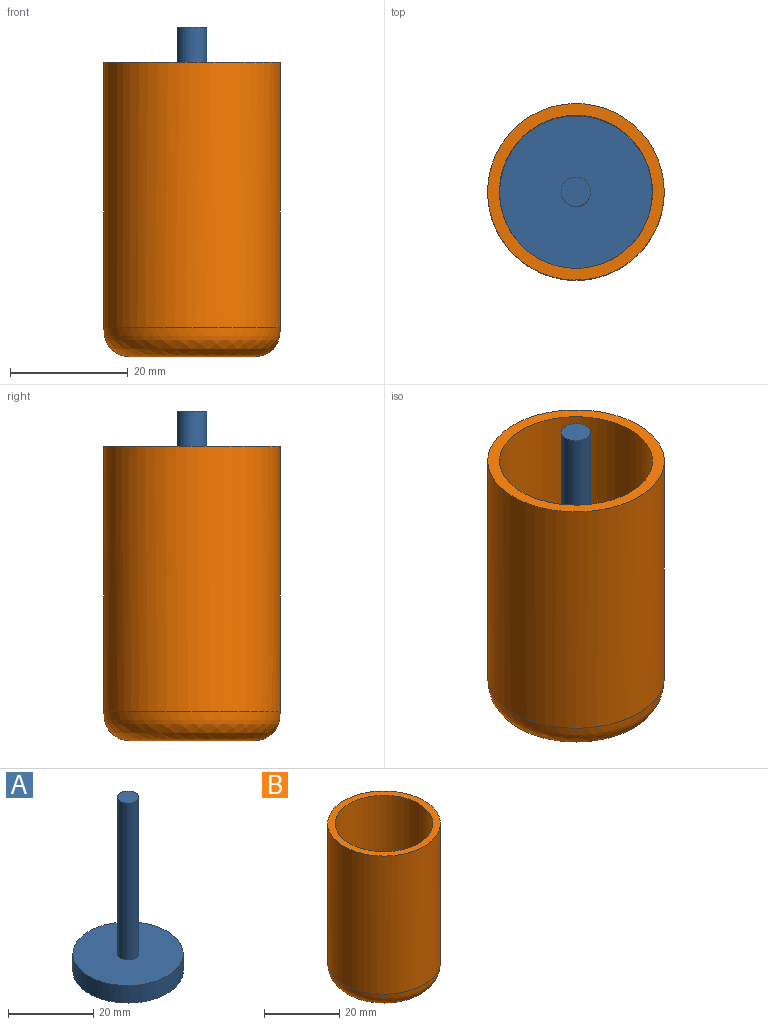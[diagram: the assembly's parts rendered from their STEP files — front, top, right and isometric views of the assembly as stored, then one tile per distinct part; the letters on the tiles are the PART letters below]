
ASSEMBLY  parts=2 mates=1
PART A: 5 faces, bbox 25.9x25.9x50 mm
  f0: cylinder r=12.95mm len=25.9mm, axis (0,0,-1), area 406.8mm2, adj f1,f2
  f1: plane 25.9x25.9mm, normal (0,0,1), area 507.2mm2, adj f0,f3
  f2: plane 25.9x25.9mm, normal (0,0,-1), area 526.9mm2, adj f0
  f3: cylinder r=2.5mm len=45mm, axis (0,0,-1), area 706.9mm2, adj f1,f4
  f4: plane 5x5mm, normal (0,0,1), area 19.6mm2, adj f3
PART B: 6 faces, bbox 30x30x50 mm
  f0: cylinder r=15mm len=45mm, axis (0,0,-1), area 4241.2mm2, adj f1,f5
  f1: plane 30x30mm, normal (0,0,1), area 175.9mm2, adj f0,f3
  f2: plane 20.01x20.01mm, normal (0,0,-1), area 314.2mm2, adj f5
  f3: cylinder r=13mm len=48mm, axis (0,0,-1), area 3920.7mm2, adj f1,f4
  f4: plane 26x26mm, normal (0,0,1), area 530.9mm2, adj f3
  f5: bspline ~30x30mm, area 677.8mm2, adj f0,f2
PLACE A t=(3.4,-14.62,19.3)mm
PLACE B t=(3.4,-14.62,25.3)mm
MATE slider A.f0 <-> B.f3  axis (0,0,-1) through (3.4,-14.62,31.3)mm
